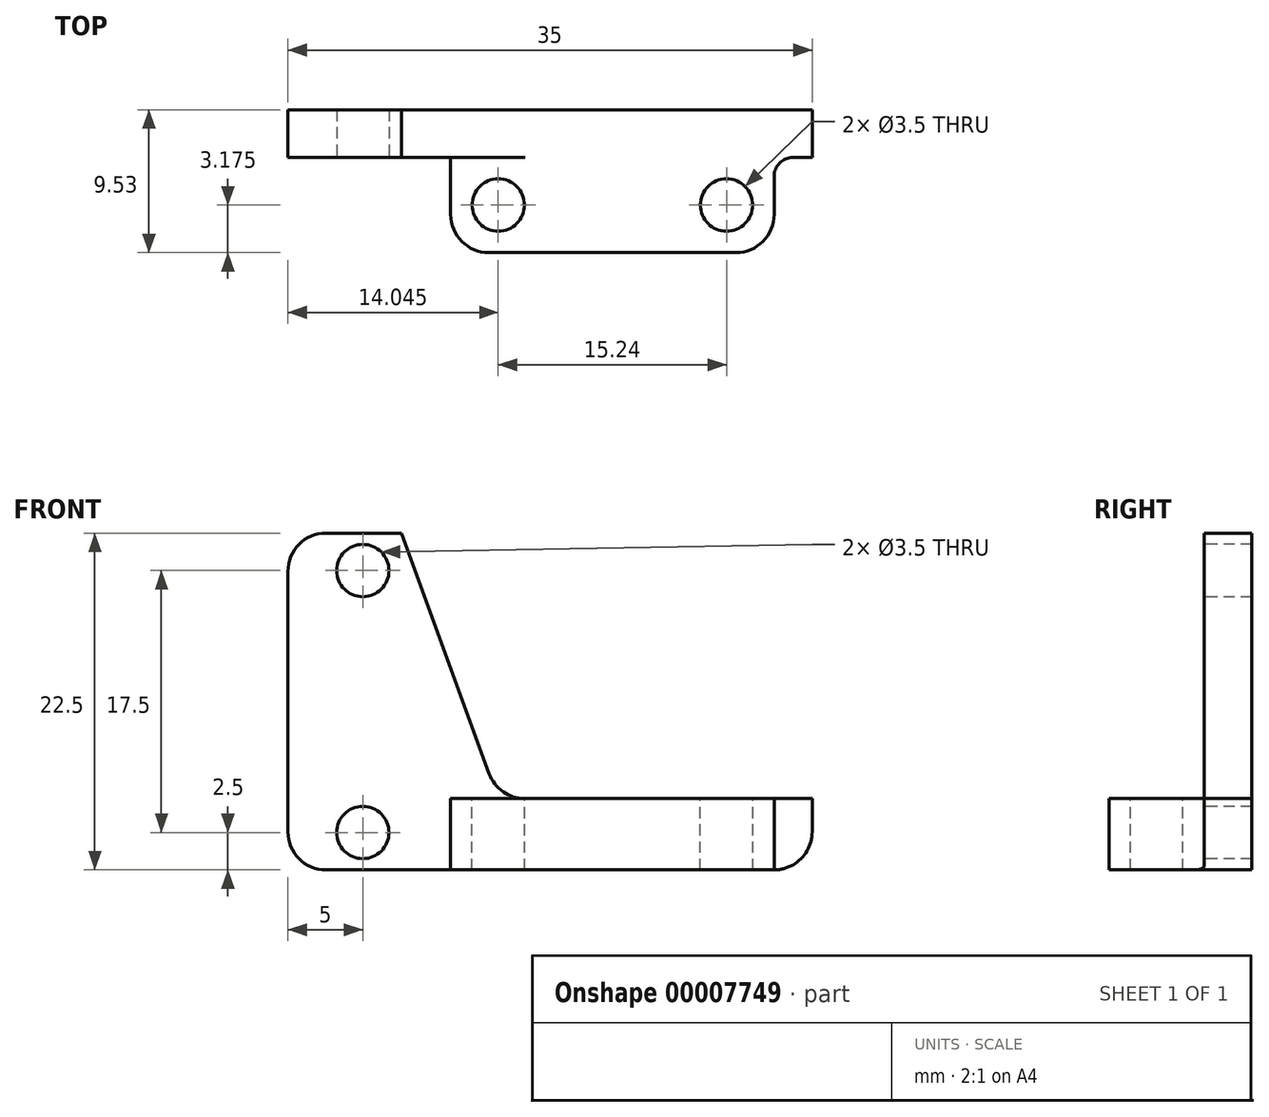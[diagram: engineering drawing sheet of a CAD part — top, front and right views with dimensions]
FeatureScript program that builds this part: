
annotation { "Feature Type Name" : "Feature", "Feature Type Description" : "" }
export const myFeature = defineFeature(function(context is Context, id is Id, definition is map)
    precondition{}
    {
        {
            var Q0;
            Q0=qCreatedBy(makeId("Front.planeOp"),FACE);
            var sketch = newSketch(context, id + "F0", { "sketchPlane" : qUnion([Q0])});
            skLineSegment(sketch, "E0.rect.bottom", {"start": v(17.5, 11.25) * mm, "end": v(-17.5, 11.25) * mm});
            skLineSegment(sketch, "E0.rect.top", {"start": v(17.5, -11.25) * mm, "end": v(-17.5, -11.25) * mm});
            skLineSegment(sketch, "E0.rect.left", {"start": v(17.5, 11.25) * mm, "end": v(17.5, -11.25) * mm});
            skLineSegment(sketch, "E0.rect.right", {"start": v(-17.5, 11.25) * mm, "end": v(-17.5, -11.25) * mm});
            skPoint(sketch, "E0.rect.middle", {"position": v(0, 0) * mm});
            skSolve(sketch);
        }
        {
            var Q0;
            Q0 = qSketchRegion(id + "F0", true);
            extrude(context, id + "F1", {"entities" : qUnion([Q0]), "oppositeDirection" : true, "depth" : 3.17 * mm});
        }
        {
            var Q0;
            Q0=makeQuery(id+"F1.opExtrude","CAP_FACE",FACE,{"disambiguationData":[OSD([sQuery(id+"F0.wireOp",EDGE,"E0.rect.bottom"),sQuery(id+"F0.wireOp",EDGE,"E0.rect.top"),sQuery(id+"F0.wireOp",EDGE,"E0.rect.left"),sQuery(id+"F0.wireOp",EDGE,"E0.rect.right")])],"isStart":true});
            var sketch = newSketch(context, id + "F2", { "sketchPlane" : qUnion([Q0])});
            skCircle(sketch, "E1", {"center": v(-12.5, 8.75) * mm, "radius": 1.75 * mm});
            skCircle(sketch, "E2.0.MirrorC", {"center": v(-12.5, -8.75) * mm, "radius": 1.75 * mm});
            skSolve(sketch);
        }
        {
            var Q0;
            Q0=makeQuery(id+"F2.imprint","IMPRINT",FACE,{"disambiguationData":[TD([[makeQuery(id+"F2.imprint","IMPRINT",EDGE,{"derivedFrom":sQuery(id+"F2.wireOp",EDGE,"E1")}),-1.0]])]});
            var sketch = newSketch(context, id + "F3", { "sketchPlane" : qUnion([Q0])});
            skLineSegment(sketch, "E3", {"start": v(17.5, -6.49) * mm, "end": v(-3.45, -6.49) * mm});
            skLineSegment(sketch, "E4", {"start": v(-3.45, -6.49) * mm, "end": v(-9.91, 11.25) * mm});
            skLineSegment(sketch, "E5", {"start": v(-9.91, 11.25) * mm, "end": v(17.5, 11.25) * mm});
            skLineSegment(sketch, "E6", {"start": v(17.5, 11.25) * mm, "end": v(17.5, -6.49) * mm});
            skSolve(sketch);
        }
        {
            var Q0;
            Q0 = qSketchRegion(id + "F3", true);
            extrude(context, id + "F4", {"entities" : qUnion([Q0]), "operationType" : NewBodyOperationType.REMOVE, "endBound" : BoundingType.THROUGH_ALL, "oppositeDirection" : true, "depth" : 25.4 * mm});
        }
        {
            var Q0;
            Q0=makeQuery(id+"F1.opExtrude","SWEPT_EDGE",EDGE,{"disambiguationData":[OSD([sQuery(id+"F0.wireOp",EDGE,"E0.rect.bottom"),sQuery(id+"F0.wireOp",EDGE,"E0.rect.right")])]});
            var Q1;
            Q1=makeQuery(id+"F1.opExtrude","SWEPT_EDGE",EDGE,{"disambiguationData":[OSD([sQuery(id+"F0.wireOp",EDGE,"E0.rect.top"),sQuery(id+"F0.wireOp",EDGE,"E0.rect.right")])]});
            var Q2;
            Q2=makeQuery(id+"F1.opExtrude","SWEPT_EDGE",EDGE,{"disambiguationData":[OSD([sQuery(id+"F0.wireOp",EDGE,"E0.rect.top"),sQuery(id+"F0.wireOp",EDGE,"E0.rect.left")])]});
            var Q3;
            Q3=makeQuery(id+"F4.boolean.opBoolean","COPY",EDGE,{"derivedFrom":makeQuery(id+"F4.opExtrude","SWEPT_EDGE",EDGE,{"disambiguationData":[OSD([sQuery(id+"F0.wireOp",EDGE,"E0.rect.left"),sQuery(id+"F3.wireOp",EDGE,"E3"),sQuery(id+"F3.wireOp",EDGE,"E6")])]})});
            var Q4;
            Q4=makeQuery(id+"F4.boolean.opBoolean","COPY",EDGE,{"derivedFrom":makeQuery(id+"F4.opExtrude","SWEPT_EDGE",EDGE,{"disambiguationData":[OSD([sQuery(id+"F3.wireOp",EDGE,"E3"),sQuery(id+"F3.wireOp",EDGE,"E4")])]})});
            var Q5;
            Q5=makeQuery(id+"F4.boolean.opBoolean","COPY",EDGE,{"derivedFrom":makeQuery(id+"F4.opExtrude","SWEPT_EDGE",EDGE,{"disambiguationData":[OSD([sQuery(id+"F0.wireOp",EDGE,"E0.rect.bottom"),sQuery(id+"F3.wireOp",EDGE,"E4"),sQuery(id+"F3.wireOp",EDGE,"E5")])]})});
            fillet(context, id + "F5", {"entities" : qUnion([Q0, Q1, Q2, Q3, Q4, Q5]), "radius" : 2.54 * mm, "tangentPropagation" : true, "allowEdgeOverflow" : false});
        }
        {
            var Q0;
            Q0 = qSketchRegion(id + "F2", true);
            extrude(context, id + "F6", {"entities" : qUnion([Q0]), "operationType" : NewBodyOperationType.REMOVE, "endBound" : BoundingType.THROUGH_ALL, "oppositeDirection" : true, "depth" : 25.4 * mm});
        }
        {
            var Q0;
            Q0=makeQuery(id+"F1.opExtrude","CAP_FACE",FACE,{"disambiguationData":[OSD([sQuery(id+"F0.wireOp",EDGE,"E0.rect.bottom"),sQuery(id+"F0.wireOp",EDGE,"E0.rect.top"),sQuery(id+"F0.wireOp",EDGE,"E0.rect.left"),sQuery(id+"F0.wireOp",EDGE,"E0.rect.right")])],"isStart":true});
            var sketch = newSketch(context, id + "F7", { "sketchPlane" : qUnion([Q0])});
            skLineSegment(sketch, "E7.bottom", {"start": v(14.96, -6.49) * mm, "end": v(-6.63, -6.49) * mm});
            skLineSegment(sketch, "E7.top", {"start": v(14.96, -11.25) * mm, "end": v(-6.63, -11.25) * mm});
            skLineSegment(sketch, "E7.left", {"start": v(14.96, -6.49) * mm, "end": v(14.96, -11.25) * mm});
            skLineSegment(sketch, "E7.right", {"start": v(-6.63, -6.49) * mm, "end": v(-6.63, -11.25) * mm});
            skSolve(sketch);
        }
        {
            var Q0;
            Q0 = qSketchRegion(id + "F7", true);
            extrude(context, id + "F8", {"entities" : qUnion([Q0]), "operationType" : NewBodyOperationType.ADD, "depth" : 6.35 * mm});
        }
        {
            var Q0;
            Q0=makeQuery(id+"F8.boolean.opBoolean","MERGE",FACE,{"derivedFrom":[makeQuery(id+"F4.boolean.opBoolean","COPY",FACE,{"derivedFrom":makeQuery(id+"F4.opExtrude","SWEPT_FACE",FACE,{"disambiguationData":[OSD([sQuery(id+"F3.wireOp",EDGE,"E3")])]})}),makeQuery(id+"F8.opExtrude","SWEPT_FACE",FACE,{"disambiguationData":[OSD([sQuery(id+"F7.wireOp",EDGE,"E7.bottom")])]})]});
            var sketch = newSketch(context, id + "F9", { "sketchPlane" : qUnion([Q0])});
            skCircle(sketch, "E8", {"center": v(11.79, -3.18) * mm, "radius": 1.75 * mm});
            skCircle(sketch, "E9", {"center": v(-3.45, -3.18) * mm, "radius": 1.75 * mm});
            skSolve(sketch);
        }
        {
            var Q0;
            Q0 = qSketchRegion(id + "F9", true);
            extrude(context, id + "F10", {"entities" : qUnion([Q0]), "operationType" : NewBodyOperationType.REMOVE, "endBound" : BoundingType.THROUGH_ALL, "oppositeDirection" : true, "depth" : 25.4 * mm});
        }
        {
            var Q0;
            Q0=makeQuery(id+"F8.opExtrude","CAP_EDGE",EDGE,{"disambiguationData":[OSD([sQuery(id+"F7.wireOp",EDGE,"E7.right")])],"isStart":false});
            var Q1;
            Q1=makeQuery(id+"FlcCyp2mqZGdAJd_1.boolean.opBoolean","COPY",EDGE,{"derivedFrom":makeQuery(id+"FlcCyp2mqZGdAJd_1.opExtrude","SWEPT_EDGE",EDGE,{"disambiguationData":[OSD([sQuery(id+"F7.wireOp",EDGE,"E7.bottom"),sQuery(id+"FPE8h0k7a6zyxRg_1.wireOp",EDGE,"c4444961-d45f-4184-82dd-7e89aab34724.bottom"),sQuery(id+"FPE8h0k7a6zyxRg_1.wireOp",EDGE,"c4444961-d45f-4184-82dd-7e89aab34724.left")])]})});
            var Q2;
            Q2=makeQuery(id+"FlcCyp2mqZGdAJd_1.boolean.opBoolean","COPY",EDGE,{"derivedFrom":makeQuery(id+"FlcCyp2mqZGdAJd_1.opExtrude","SWEPT_EDGE",EDGE,{"disambiguationData":[OSD([sQuery(id+"F7.wireOp",EDGE,"E7.bottom"),sQuery(id+"FPE8h0k7a6zyxRg_1.wireOp",EDGE,"c4444961-d45f-4184-82dd-7e89aab34724.top"),sQuery(id+"FPE8h0k7a6zyxRg_1.wireOp",EDGE,"c4444961-d45f-4184-82dd-7e89aab34724.left")])]})});
            var Q3;
            Q3=makeQuery(id+"FlcCyp2mqZGdAJd_1.boolean.opBoolean","COPY",EDGE,{"derivedFrom":makeQuery(id+"FlcCyp2mqZGdAJd_1.opExtrude","SWEPT_EDGE",EDGE,{"disambiguationData":[OSD([sQuery(id+"F7.wireOp",EDGE,"E7.bottom"),sQuery(id+"FPE8h0k7a6zyxRg_1.wireOp",EDGE,"c4444961-d45f-4184-82dd-7e89aab34724.bottom"),sQuery(id+"FPE8h0k7a6zyxRg_1.wireOp",EDGE,"c4444961-d45f-4184-82dd-7e89aab34724.right")])]})});
            var Q4;
            Q4=makeQuery(id+"F8.opExtrude","CAP_EDGE",EDGE,{"disambiguationData":[OSD([sQuery(id+"F7.wireOp",EDGE,"E7.left")])],"isStart":false});
            var Q5;
            Q5=makeQuery(id+"FlcCyp2mqZGdAJd_1.boolean.opBoolean","COPY",EDGE,{"derivedFrom":makeQuery(id+"FlcCyp2mqZGdAJd_1.opExtrude","SWEPT_EDGE",EDGE,{"disambiguationData":[OSD([sQuery(id+"FPE8h0k7a6zyxRg_1.wireOp",EDGE,"c4444961-d45f-4184-82dd-7e89aab34724.top"),sQuery(id+"FPE8h0k7a6zyxRg_1.wireOp",EDGE,"c4444961-d45f-4184-82dd-7e89aab34724.right")])]})});
            var Q6;
            Q6=makeQuery(id+"F8.opExtrude","CAP_EDGE",EDGE,{"disambiguationData":[OSD([sQuery(id+"F7.wireOp",EDGE,"E7.right")])],"isStart":true});
            fillet(context, id + "F11", {"entities" : qUnion([Q0, Q1, Q2, Q3, Q4, Q5, Q6]), "radius" : 2.54 * mm, "tangentPropagation" : true, "allowEdgeOverflow" : false});
        }
        {
            var Q0;
            Q0=makeQuery(id+"F8.opExtrude","CAP_EDGE",EDGE,{"disambiguationData":[OSD([sQuery(id+"F7.wireOp",EDGE,"E7.left")])],"isStart":true});
            fillet(context, id + "F12", {"entities" : qUnion([Q0]), "radius" : 1.27 * mm, "tangentPropagation" : true, "allowEdgeOverflow" : false});
        }
    });
